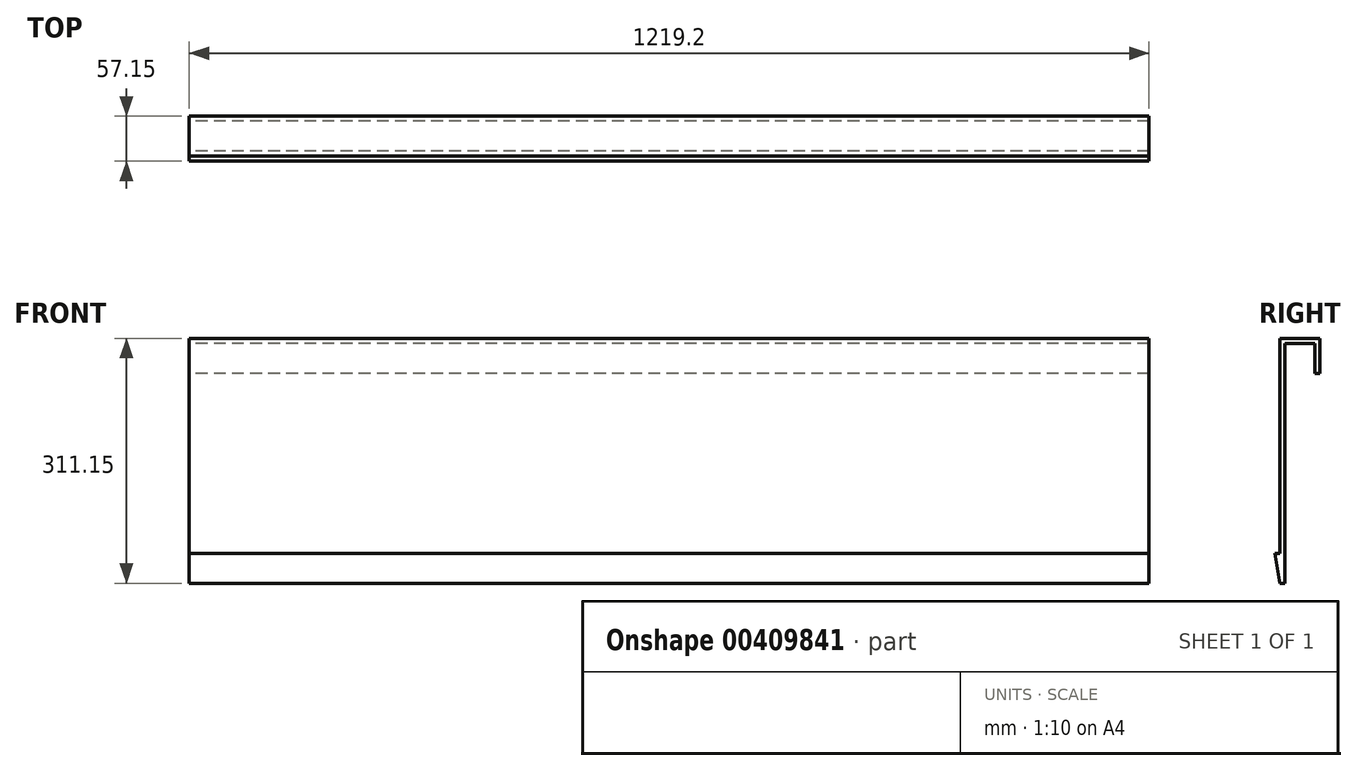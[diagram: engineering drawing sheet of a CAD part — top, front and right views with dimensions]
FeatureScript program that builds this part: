
annotation { "Feature Type Name" : "Feature", "Feature Type Description" : "" }
export const myFeature = defineFeature(function(context is Context, id is Id, definition is map)
    precondition{}
    {
        {
            var Q0;
            Q0=qCreatedBy(makeId("Right.planeOp"),FACE);
            var sketch = newSketch(context, id + "F0", { "sketchPlane" : qUnion([Q0])});
            skLineSegment(sketch, "E0", {"start": v(-44.45, 159.91) * mm, "end": v(-44.45, -144.89) * mm});
            skLineSegment(sketch, "E1", {"start": v(-44.45, 159.91) * mm, "end": v(-6.35, 159.91) * mm});
            skLineSegment(sketch, "E2", {"start": v(-6.35, 159.91) * mm, "end": v(-6.35, 121.81) * mm});
            skLineSegment(sketch, "E3", {"start": v(-44.45, -144.89) * mm, "end": v(-50.8, -144.89) * mm});
            skLineSegment(sketch, "E4", {"start": v(-50.8, -144.89) * mm, "end": v(-50.8, 166.26) * mm});
            skLineSegment(sketch, "E5", {"start": v(-50.8, 166.26) * mm, "end": v(0, 166.26) * mm});
            skLineSegment(sketch, "E6", {"start": v(0, 166.26) * mm, "end": v(0, 121.81) * mm});
            skLineSegment(sketch, "E7", {"start": v(0, 121.81) * mm, "end": v(-6.35, 121.81) * mm});
            skPoint(sketch, "E8", {"position": v(-50.8, -106.79) * mm});
            skLineSegment(sketch, "E9", {"start": v(-50.8, -144.89) * mm, "end": v(-57.15, -106.79) * mm});
            skLineSegment(sketch, "E10", {"start": v(-57.15, -106.79) * mm, "end": v(-50.8, -106.79) * mm});
            skSolve(sketch);
        }
        {
            var Q0;
            Q0=makeQuery(id+"F0.imprint","IMPRINT",FACE,{"disambiguationData":[TD([[makeQuery(id+"F0.imprint","IMPRINT",EDGE,{"derivedFrom":sQuery(id+"F0.wireOp",EDGE,"E0")}),-1.0]])]});
            extrude(context, id + "F1", {"entities" : qUnion([Q0]), "depth" : 1219.2 * mm});
        }
        {
            var Q0;
            {var subQ0=sQuery(id+"F0.wireOp",EDGE,"E9");Q0=makeQuery(id+"F0.imprint","IMPRINT",FACE,{"disambiguationData":[TD([[makeQuery(id+"F0.imprint","IMPRINT",EDGE,{"derivedFrom":subQ0}),-1.0]])]});}
            extrude(context, id + "F2", {"entities" : qUnion([Q0]), "operationType" : NewBodyOperationType.ADD, "depth" : 1219.2 * mm});
        }
    });
